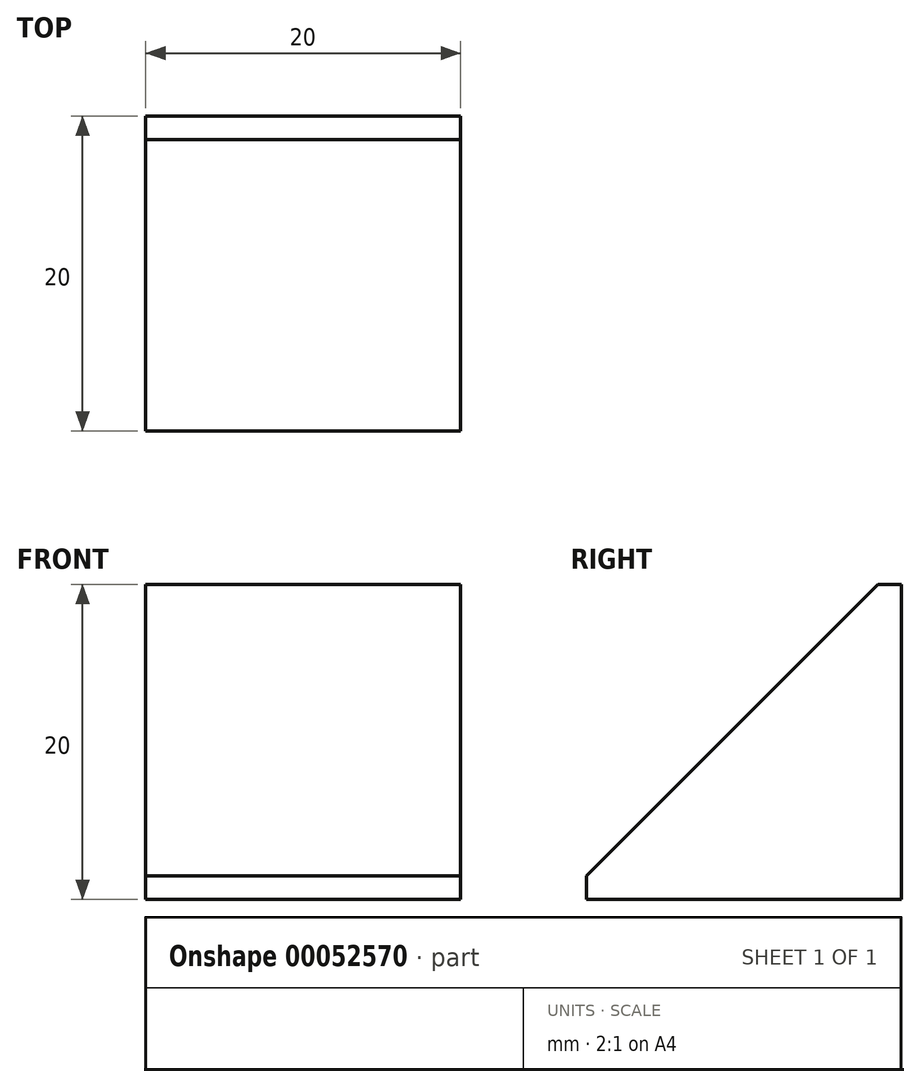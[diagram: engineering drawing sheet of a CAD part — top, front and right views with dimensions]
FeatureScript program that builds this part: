
annotation { "Feature Type Name" : "Feature", "Feature Type Description" : "" }
export const myFeature = defineFeature(function(context is Context, id is Id, definition is map)
    precondition{}
    {
        {
            var Q0;
            Q0=qCreatedBy(makeId("Right.planeOp"),FACE);
            var sketch = newSketch(context, id + "F0", { "sketchPlane" : qUnion([Q0])});
            skLineSegment(sketch, "E0", {"start": v(0, 0) * mm, "end": v(0, 20) * mm});
            skLineSegment(sketch, "E1", {"start": v(0, 20) * mm, "end": v(-1.5, 20) * mm});
            skLineSegment(sketch, "E2", {"start": v(-1.5, 20) * mm, "end": v(-20, 1.5) * mm});
            skLineSegment(sketch, "E3", {"start": v(-20, 1.5) * mm, "end": v(-20, 0) * mm});
            skLineSegment(sketch, "E4", {"start": v(-20, 0) * mm, "end": v(0, 0) * mm});
            skSolve(sketch);
        }
        {
            var Q0;
            Q0=makeQuery(id+"F0.imprint","IMPRINT",FACE,{"disambiguationData":[TD([[makeQuery(id+"F0.imprint","IMPRINT",EDGE,{"derivedFrom":sQuery(id+"F0.wireOp",EDGE,"E0")}),1.0]])]});
            extrude(context, id + "F1", {"entities" : qUnion([Q0]), "endBound" : BoundingType.SYMMETRIC, "depth" : 20 * mm});
        }
    });
